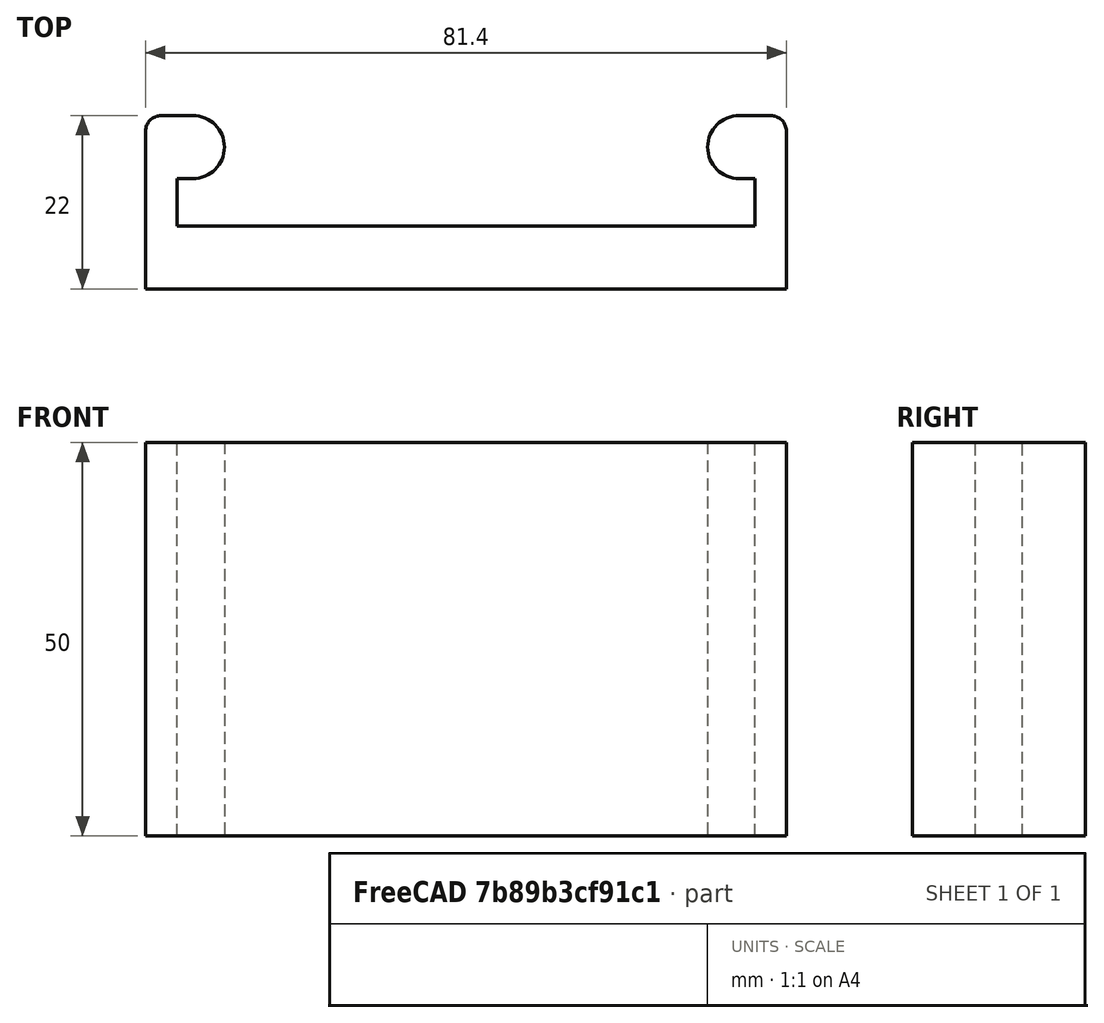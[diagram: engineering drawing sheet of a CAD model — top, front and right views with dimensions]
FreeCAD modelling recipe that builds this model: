
FCSTD DOCUMENT  (FreeCAD 0.19R24291 (Git))
Label: smdmagazinerail
License: All rights reserved
LicenseURL: http://en.wikipedia.org/wiki/All_rights_reserved
objects: Sketcher::SketchObject×1, PartDesign::Pad×1, PartDesign::Body×1
note: 4 computed .brp shape members not serialized (recipe doc carries the construction recipe); baked Part::Feature solids carry a one-line shape summary decoded from their .brp

FEATURE [Sketcher::SketchObject] Sketch
  FullyConstrained = true
  MapMode = 5
  Support = -> [XY_Plane]
  sketch-geometry (17):
    g0: ArcOfCircle CenterX=-34.7 CenterY=18 CenterZ=0 NormalX=0 NormalY=0 NormalZ=1 AngleXU=0 Radius=4 StartAngle=4.71239 EndAngle=7.85398
    g1: ArcOfCircle CenterX=34.7 CenterY=18 CenterZ=0 NormalX=0 NormalY=0 NormalZ=1 AngleXU=0 Radius=4 StartAngle=1.5708 EndAngle=4.71239
    g2: LineSegment StartX=34.7 StartY=22 StartZ=0 EndX=38.7 EndY=22 EndZ=0
    g3: LineSegment StartX=40.7 StartY=20 StartZ=0 EndX=40.7 EndY=0 EndZ=0
    g4: LineSegment StartX=40.7 StartY=0 StartZ=0 EndX=0 EndY=0 EndZ=0
    g5: LineSegment StartX=0 StartY=0 StartZ=0 EndX=-40.7 EndY=0 EndZ=0
    g6: LineSegment StartX=-40.7 StartY=0 StartZ=0 EndX=-40.7 EndY=20 EndZ=0
    g7: LineSegment StartX=-38.7 StartY=22 StartZ=0 EndX=-34.7 EndY=22 EndZ=0
    g8: LineSegment StartX=-34.7 StartY=14 StartZ=0 EndX=-36.7 EndY=14 EndZ=0
    g9: LineSegment StartX=-36.7 StartY=14 StartZ=0 EndX=-36.7 EndY=8 EndZ=0
    g10: LineSegment StartX=-36.7 StartY=8 StartZ=0 EndX=36.7 EndY=8 EndZ=0
    g11: LineSegment StartX=34.7 StartY=14 StartZ=0 EndX=36.7 EndY=14 EndZ=0
    g12: LineSegment StartX=36.7 StartY=14 StartZ=0 EndX=36.7 EndY=8 EndZ=0
    g13: ArcOfCircle CenterX=38.7 CenterY=20 CenterZ=0 NormalX=0 NormalY=0 NormalZ=1 AngleXU=0 Radius=2 StartAngle=-9e-16 EndAngle=1.5708
    g14: GeomPoint X=40.7 Y=22 Z=0
    g15: ArcOfCircle CenterX=-38.7 CenterY=20 CenterZ=0 NormalX=0 NormalY=0 NormalZ=1 AngleXU=0 Radius=2 StartAngle=1.5708 EndAngle=3.14159
    g16: GeomPoint X=-40.7 Y=22 Z=0
  constraints (48):
    c: Coincident(g2,g1)
    c: Horizontal(g2)
    c: PointOnObject(g3,g-1)
    c: Vertical(g3)
    c: Coincident(g4,g3)
    c: Coincident(g4,g-1)
    c: Coincident(g5,g4)
    c: PointOnObject(g5,g-1)
    c: Coincident(g6,g5)
    c: Vertical(g6)
    c: Coincident(g8,g0)
    c: Coincident(g9,g8)
    c: Vertical(g9)
    c: Coincident(g10,g9)
    c: Horizontal(g10)
    c: Equal(g4,g5)
    c: Equal(g1,g0)
    c: Coincident(g11,g1)
    c: Coincident(g12,g11)
    c: Coincident(g12,g10)
    c: Equal(g8,g11)
    c: Horizontal(g8)
    c: Vertical(g12)
    c: Equal(g12,g9)
    c: Horizontal(g11)
    c: Diameter(g0) = 8
    c: DistanceY(g10,g1) = 10
    c: DistanceX(g0,g1) = 69.4
    c: DistanceX(g10,g3) = 4
    c: DistanceY(g3,g10) = 8
    c: DistanceX(g11,g11) = 2
    c: Vertical(g1,g1)
    c: Vertical(g1,g1)
    c: Coincident(g7,g0)
    c: Horizontal(g7)
    c: Vertical(g0,g0)
    c: Vertical(g0,g0)
    c: PointOnObject(g14,g2)
    c: PointOnObject(g14,g3)
    c: Tangent(g2,g13) = 1.5708
    c: Tangent(g3,g13) = 1.5708
    c: PointOnObject(g16,g7)
    c: PointOnObject(g16,g6)
    c: Tangent(g7,g15) = 1.5708
    c: Tangent(g6,g15) = 1.5708
    c: Equal(g13,g15)
    c: Radius(g13) = 2
    c: Equal(g2,g7)
FEATURE [PartDesign::Pad] Pad
  Direction = (1,1,1)
  Length = 50
  Length2 = 100
  Profile = -> Sketch
  Type = 0
FEATURE [PartDesign::Body] Body
  Group = -> [Sketch,Pad]
  Origin = -> Origin
  Tip = -> Pad
